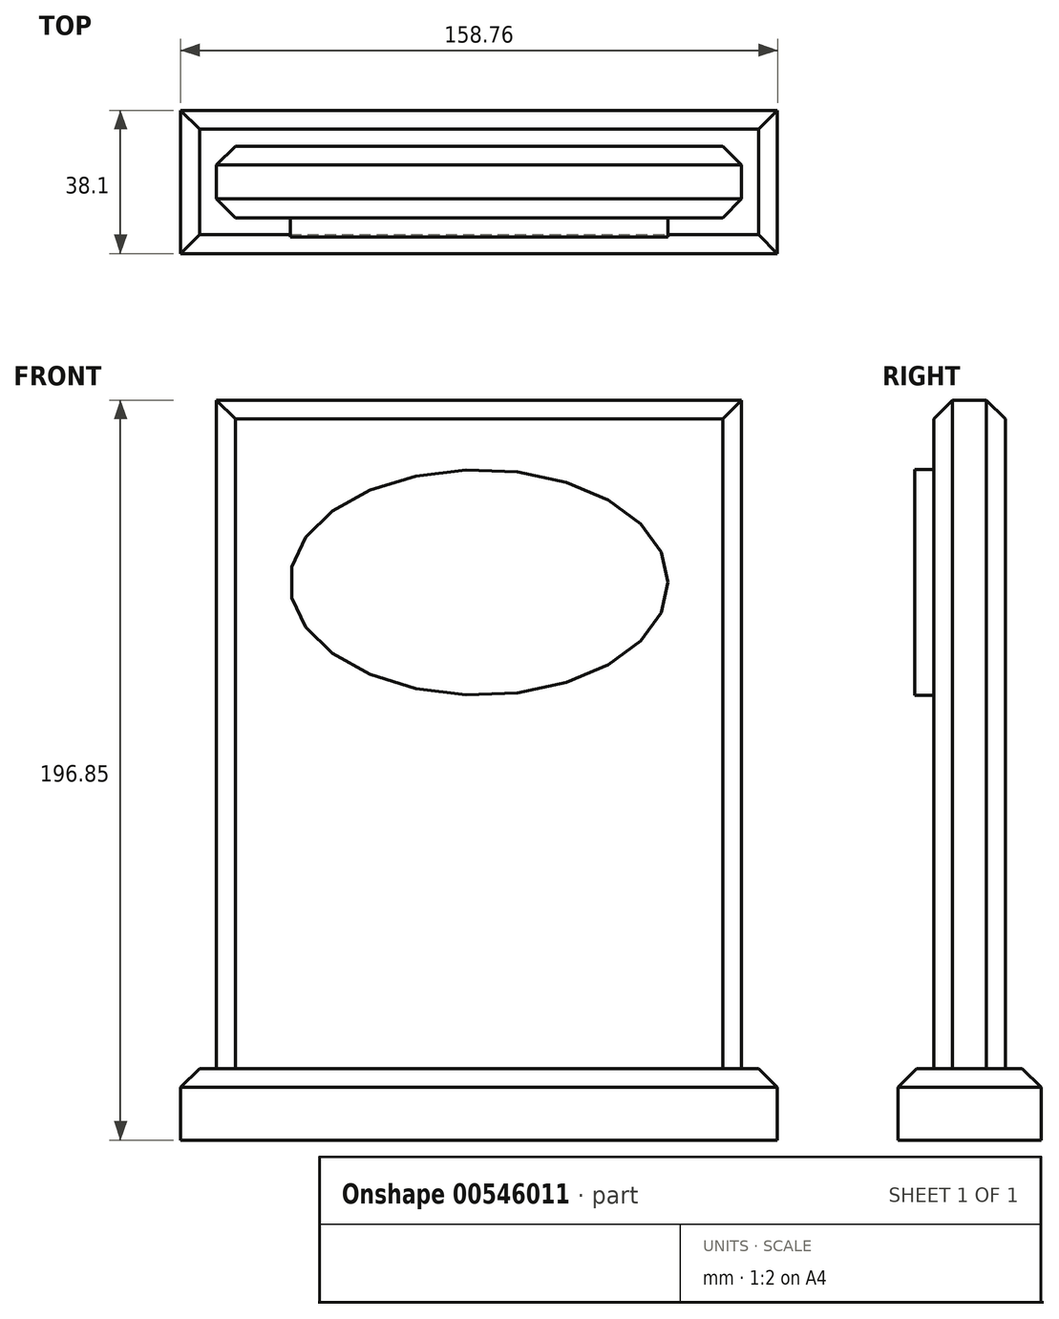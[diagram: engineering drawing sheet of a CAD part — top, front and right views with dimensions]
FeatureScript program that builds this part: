
annotation { "Feature Type Name" : "Feature", "Feature Type Description" : "" }
export const myFeature = defineFeature(function(context is Context, id is Id, definition is map)
    precondition{}
    {
        {
            var Q0;
            Q0=qCreatedBy(makeId("Top.planeOp"),FACE);
            var sketch = newSketch(context, id + "F0", { "sketchPlane" : qUnion([Q0])});
            skLineSegment(sketch, "E0.bottom", {"start": v(79.38, 19.05) * mm, "end": v(-79.38, 19.05) * mm});
            skLineSegment(sketch, "E0.top", {"start": v(79.38, -19.05) * mm, "end": v(-79.38, -19.05) * mm});
            skLineSegment(sketch, "E0.left", {"start": v(79.38, 19.05) * mm, "end": v(79.38, -19.05) * mm});
            skLineSegment(sketch, "E0.right", {"start": v(-79.38, 19.05) * mm, "end": v(-79.38, -19.05) * mm});
            skPoint(sketch, "E0.middle", {"position": v(0, 0) * mm});
            skSolve(sketch);
        }
        {
            var Q0;
            Q0=makeQuery(id+"F0.imprint","IMPRINT",FACE,{"disambiguationData":[TD([[makeQuery(id+"F0.imprint","IMPRINT",EDGE,{"derivedFrom":sQuery(id+"F0.wireOp",EDGE,"E0.bottom")}),1.0]])]});
            extrude(context, id + "F1", {"entities" : qUnion([Q0]), "depth" : 19.05 * mm, "offsetDistance" : 25 * mm});
        }
        {
            var Q0;
            Q0=makeQuery(id+"F1.opExtrude","CAP_FACE",FACE,{"disambiguationData":[OSD([sQuery(id+"F0.wireOp",EDGE,"E0.bottom"),sQuery(id+"F0.wireOp",EDGE,"E0.top"),sQuery(id+"F0.wireOp",EDGE,"E0.left"),sQuery(id+"F0.wireOp",EDGE,"E0.right")])],"isStart":false});
            var sketch = newSketch(context, id + "F2", { "sketchPlane" : qUnion([Q0])});
            skLineSegment(sketch, "E1.bottom", {"start": v(69.85, 9.53) * mm, "end": v(-69.85, 9.53) * mm});
            skLineSegment(sketch, "E1.top", {"start": v(69.85, -9.52) * mm, "end": v(-69.85, -9.52) * mm});
            skLineSegment(sketch, "E1.left", {"start": v(69.85, 9.53) * mm, "end": v(69.85, -9.52) * mm});
            skLineSegment(sketch, "E1.right", {"start": v(-69.85, 9.53) * mm, "end": v(-69.85, -9.52) * mm});
            skPoint(sketch, "E1.middle", {"position": v(0, 0) * mm});
            skSolve(sketch);
        }
        {
            var Q0;
            Q0=makeQuery(id+"F2.imprint","IMPRINT",FACE,{"disambiguationData":[TD([[makeQuery(id+"F2.imprint","IMPRINT",EDGE,{"derivedFrom":sQuery(id+"F2.wireOp",EDGE,"E1.bottom")}),1.0]])]});
            extrude(context, id + "F3", {"entities" : qUnion([Q0]), "operationType" : NewBodyOperationType.ADD, "depth" : 177.8 * mm, "offsetDistance" : 25 * mm});
        }
        {
            var Q0;
            Q0=makeQuery(id+"F1.opExtrude","CAP_EDGE",EDGE,{"disambiguationData":[OSD([sQuery(id+"F0.wireOp",EDGE,"E0.top")])],"isStart":false});
            var Q1;
            Q1=makeQuery(id+"F1.opExtrude","CAP_EDGE",EDGE,{"disambiguationData":[OSD([sQuery(id+"F0.wireOp",EDGE,"E0.right")])],"isStart":false});
            var Q2;
            Q2=makeQuery(id+"F1.opExtrude","CAP_EDGE",EDGE,{"disambiguationData":[OSD([sQuery(id+"F0.wireOp",EDGE,"E0.left")])],"isStart":false});
            var Q3;
            Q3=makeQuery(id+"F1.opExtrude","CAP_EDGE",EDGE,{"disambiguationData":[OSD([sQuery(id+"F0.wireOp",EDGE,"E0.bottom")])],"isStart":false});
            var Q4;
            Q4=makeQuery(id+"F3.opExtrude","SWEPT_EDGE",EDGE,{"disambiguationData":[OSD([sQuery(id+"F2.wireOp",EDGE,"E1.top"),sQuery(id+"F2.wireOp",EDGE,"E1.right")])]});
            var Q5;
            Q5=makeQuery(id+"F3.opExtrude","SWEPT_EDGE",EDGE,{"disambiguationData":[OSD([sQuery(id+"F2.wireOp",EDGE,"E1.bottom"),sQuery(id+"F2.wireOp",EDGE,"E1.right")])]});
            var Q6;
            Q6=makeQuery(id+"F3.opExtrude","CAP_EDGE",EDGE,{"disambiguationData":[OSD([sQuery(id+"F2.wireOp",EDGE,"E1.top")])],"isStart":false});
            var Q7;
            Q7=makeQuery(id+"F3.opExtrude","CAP_EDGE",EDGE,{"disambiguationData":[OSD([sQuery(id+"F2.wireOp",EDGE,"E1.bottom")])],"isStart":false});
            var Q8;
            Q8=makeQuery(id+"F3.opExtrude","SWEPT_EDGE",EDGE,{"disambiguationData":[OSD([sQuery(id+"F2.wireOp",EDGE,"E1.top"),sQuery(id+"F2.wireOp",EDGE,"E1.left")])]});
            var Q9;
            Q9=makeQuery(id+"F3.opExtrude","SWEPT_EDGE",EDGE,{"disambiguationData":[OSD([sQuery(id+"F2.wireOp",EDGE,"E1.bottom"),sQuery(id+"F2.wireOp",EDGE,"E1.left")])]});
            chamfer(context, id + "F4", {"entities" : qUnion([Q0, Q1, Q2, Q3, Q4, Q5, Q6, Q7, Q8, Q9]), "width" : 5 * mm, "tangentPropagation" : true});
        }
        {
            var Q0;
            Q0=makeQuery(id+"F3.opExtrude","SWEPT_FACE",FACE,{"disambiguationData":[OSD([sQuery(id+"F2.wireOp",EDGE,"E1.top")])]});
            var sketch = newSketch(context, id + "F5", { "sketchPlane" : qUnion([Q0])});
            skEllipse(sketch, "E2", {"center": v(0, 148.37) * mm, "majorRadius": 50.27 * mm, "minorRadius": 30 * mm, "majorAxis": v(1, 0)});
            skText(sketch, "E3", { "text": "CAPTURE THE FLAG", "fontName": "Tinos-Bold.ttf"});
            skLineSegment(sketch, "E4", {"start": v(0, 191.85) * mm, "end": v(0, 19.05) * mm, "construction": true});
            skText(sketch, "E5", { "text": "CHAMPION", "fontName": "Tinos-Bold.ttf"});
            skText(sketch, "E6", { "text": "2017", "fontName": "Tinos-Bold.ttf"});
            skLineSegment(sketch, "E7.0", {"start": v(-69.85, 196.85) * mm, "end": v(69.85, 196.85) * mm});
            skLineSegment(sketch, "E7.1", {"start": v(69.85, 196.85) * mm, "end": v(69.85, 19.05) * mm});
            skLineSegment(sketch, "E7.2", {"start": v(-69.85, 19.05) * mm, "end": v(-69.85, 196.85) * mm});
            skLineSegment(sketch, "E7.3", {"start": v(69.85, 19.05) * mm, "end": v(-69.85, 19.05) * mm});
            const initialGuessF5  = {"E3": [-0.06, 0.09405, 1, 0, 0.00842], "E5": [-0.05, 0.06905, 1, 0, 0.0126], "E6": [-0.03616, 0.02905, 1, 0, 0.02775]};
            skSetInitialGuess(sketch, initialGuessF5);
            skSolve(sketch);
        }
        {
            var Q0;
            Q0=makeQuery(id+"F5.imprint","IMPRINT",FACE,{"disambiguationData":[TD([[makeQuery(id+"F5.imprint","IMPRINT",EDGE,{"derivedFrom":sQuery(id+"F5.wireOp",EDGE,"E2")}),1.0]])]});
            var Q1;
            Q1=sQuery(id+"F5.wireOp",EDGE,"E2");
            extrude(context, id + "F6", {"entities" : qUnion([Q0]), "surfaceEntities" : qUnion([Q1]), "depth" : 5.08 * mm, "offsetDistance" : 25 * mm});
        }
    });
